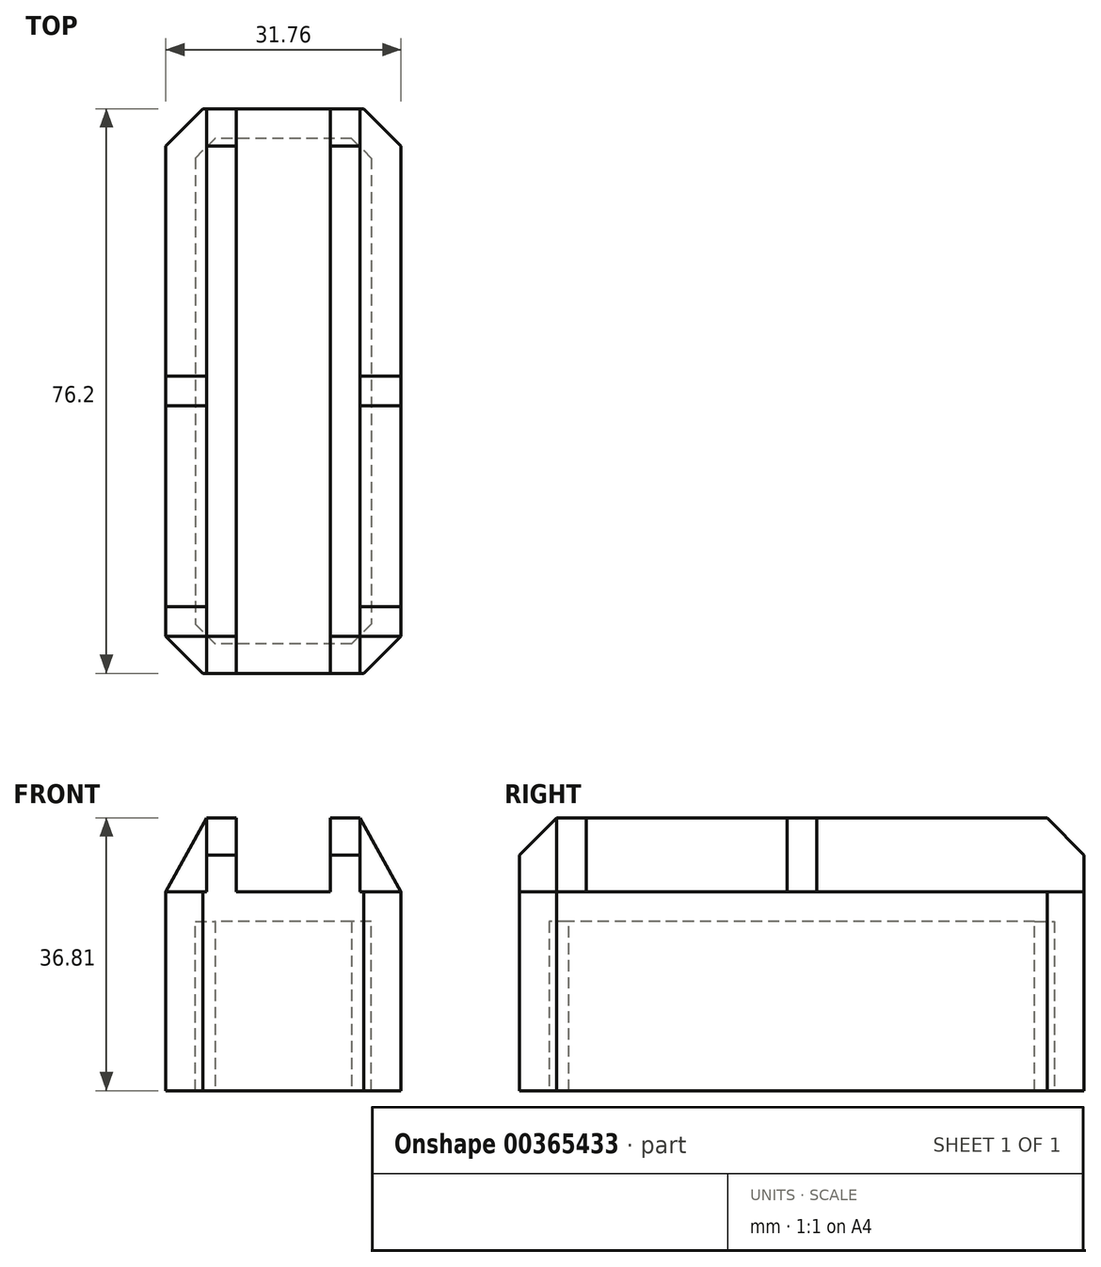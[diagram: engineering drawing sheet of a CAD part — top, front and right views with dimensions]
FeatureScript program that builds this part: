
annotation { "Feature Type Name" : "Feature", "Feature Type Description" : "" }
export const myFeature = defineFeature(function(context is Context, id is Id, definition is map)
    precondition{}
    {
        {
            var Q0;
            Q0=qCreatedBy(makeId("Top.planeOp"),FACE);
            var sketch = newSketch(context, id + "F0", { "sketchPlane" : qUnion([Q0])});
            skLineSegment(sketch, "E0.bottom", {"start": v(15.88, 38.1) * mm, "end": v(-15.87, 38.1) * mm});
            skLineSegment(sketch, "E0.top", {"start": v(15.87, -38.1) * mm, "end": v(-15.88, -38.1) * mm});
            skLineSegment(sketch, "E0.left", {"start": v(15.88, 38.1) * mm, "end": v(15.88, -38.1) * mm});
            skLineSegment(sketch, "E0.right", {"start": v(-15.87, 38.1) * mm, "end": v(-15.88, -38.1) * mm});
            skPoint(sketch, "E0.middle", {"position": v(0, 0) * mm});
            skSolve(sketch);
        }
        {
            var Q0;
            Q0=makeQuery(id+"F0.imprint","IMPRINT",FACE,{"disambiguationData":[TD([[makeQuery(id+"F0.imprint","IMPRINT",EDGE,{"derivedFrom":sQuery(id+"F0.wireOp",EDGE,"E0.bottom")}),1.0]])]});
            extrude(context, id + "F1", {"entities" : qUnion([Q0]), "oppositeDirection" : true, "depth" : 26.8 * mm});
        }
        {
            var Q0;
            Q0=makeQuery(id+"F1.opExtrude","SWEPT_EDGE",EDGE,{"disambiguationData":[OSD([sQuery(id+"F0.wireOp",EDGE,"E0.top"),sQuery(id+"F0.wireOp",EDGE,"E0.right")])]});
            var Q1;
            Q1=makeQuery(id+"F1.opExtrude","SWEPT_EDGE",EDGE,{"disambiguationData":[OSD([sQuery(id+"F0.wireOp",EDGE,"E0.top"),sQuery(id+"F0.wireOp",EDGE,"E0.left")])]});
            var Q2;
            Q2=makeQuery(id+"F1.opExtrude","SWEPT_EDGE",EDGE,{"disambiguationData":[OSD([sQuery(id+"F0.wireOp",EDGE,"E0.bottom"),sQuery(id+"F0.wireOp",EDGE,"E0.right")])]});
            var Q3;
            Q3=makeQuery(id+"F1.opExtrude","SWEPT_EDGE",EDGE,{"disambiguationData":[OSD([sQuery(id+"F0.wireOp",EDGE,"E0.bottom"),sQuery(id+"F0.wireOp",EDGE,"E0.left")])]});
            chamfer(context, id + "F2", {"entities" : qUnion([Q0, Q1, Q2, Q3]), "width" : 5 * mm, "tangentPropagation" : true});
        }
        {
            var Q0;
            Q0=makeQuery(id+"F1.opExtrude","CAP_FACE",FACE,{"disambiguationData":[OSD([sQuery(id+"F0.wireOp",EDGE,"E0.bottom"),sQuery(id+"F0.wireOp",EDGE,"E0.top"),sQuery(id+"F0.wireOp",EDGE,"E0.left"),sQuery(id+"F0.wireOp",EDGE,"E0.right")])],"isStart":false});
            shell(context, id + "F3", {"entities" : qUnion([Q0]), "thickness" : 4 * mm});
        }
        {
            var Q0;
            Q0=qCreatedBy(makeId("Front.planeOp"),FACE);
            var sketch = newSketch(context, id + "F4", { "sketchPlane" : qUnion([Q0])});
            skLineSegment(sketch, "E1.bottom", {"start": v(-10.35, 10) * mm, "end": v(-6.35, 10) * mm});
            skLineSegment(sketch, "E1.top", {"start": v(-10.35, 0) * mm, "end": v(-6.35, 0) * mm});
            skLineSegment(sketch, "E1.left", {"start": v(-10.35, 10) * mm, "end": v(-10.35, 0) * mm});
            skLineSegment(sketch, "E1.right", {"start": v(-6.35, 10) * mm, "end": v(-6.35, 0) * mm});
            skLineSegment(sketch, "E2", {"start": v(0, 9.11) * mm, "end": v(0, -8.98) * mm, "construction": true});
            skLineSegment(sketch, "E3.MirrorCS", {"start": v(10.35, 10) * mm, "end": v(6.35, 10) * mm});
            skLineSegment(sketch, "E4.MirrorCS", {"start": v(10.35, 10) * mm, "end": v(10.35, 0) * mm});
            skLineSegment(sketch, "E5.MirrorCS", {"start": v(6.35, 10) * mm, "end": v(6.35, 0) * mm});
            skLineSegment(sketch, "E6.MirrorCS", {"start": v(10.35, 0) * mm, "end": v(6.35, 0) * mm});
            skSolve(sketch);
        }
        {
            var Q0;
            Q0=makeQuery(id+"F4.imprint","IMPRINT",FACE,{"disambiguationData":[TD([[makeQuery(id+"F4.imprint","IMPRINT",EDGE,{"derivedFrom":sQuery(id+"F4.wireOp",EDGE,"E3.MirrorCS")}),1.0]])]});
            var Q1;
            Q1=makeQuery(id+"F4.imprint","IMPRINT",FACE,{"disambiguationData":[TD([[makeQuery(id+"F4.imprint","IMPRINT",EDGE,{"derivedFrom":sQuery(id+"F4.wireOp",EDGE,"E1.bottom")}),-1.0]])]});
            extrude(context, id + "F5", {"entities" : qUnion([Q0, Q1]), "operationType" : NewBodyOperationType.ADD, "endBound" : BoundingType.SYMMETRIC, "depth" : 76.2 * mm});
        }
        {
            var Q0;
            Q0=qCreatedBy(makeId("Front.planeOp"),FACE);
            var sketch = newSketch(context, id + "F6", { "sketchPlane" : qUnion([Q0])});
            skLineSegment(sketch, "E7", {"start": v(-10.35, 0) * mm, "end": v(-10.35, 10) * mm});
            skLineSegment(sketch, "E8", {"start": v(-10.35, 0) * mm, "end": v(-15.88, 0) * mm});
            skLineSegment(sketch, "E9", {"start": v(-10.35, 10) * mm, "end": v(-15.88, 0) * mm});
            skLineSegment(sketch, "E10", {"start": v(0, 0) * mm, "end": v(0, 13.7) * mm, "construction": true});
            skLineSegment(sketch, "E11.MirrorCS", {"start": v(10.35, 10) * mm, "end": v(15.88, 0) * mm});
            skLineSegment(sketch, "E12.MirrorCS", {"start": v(10.35, 0) * mm, "end": v(15.88, 0) * mm});
            skLineSegment(sketch, "E13.MirrorCS", {"start": v(10.35, 0) * mm, "end": v(10.35, 10) * mm});
            skSolve(sketch);
        }
        {
            var Q0;
            Q0=makeQuery(id+"F6.imprint","IMPRINT",FACE,{"disambiguationData":[TD([[makeQuery(id+"F6.imprint","IMPRINT",EDGE,{"derivedFrom":sQuery(id+"F6.wireOp",EDGE,"E7")}),1.0]])]});
            var Q1;
            Q1=makeQuery(id+"F6.imprint","IMPRINT",FACE,{"disambiguationData":[TD([[makeQuery(id+"F6.imprint","IMPRINT",EDGE,{"derivedFrom":sQuery(id+"F6.wireOp",EDGE,"E11.MirrorCS")}),-1.0]])]});
            extrude(context, id + "F7", {"entities" : qUnion([Q0, Q1]), "operationType" : NewBodyOperationType.ADD, "endBound" : BoundingType.SYMMETRIC, "depth" : 4 * mm});
        }
        {
            var Q0;
            Q0=qCreatedBy(makeId("Front.planeOp"),FACE);
            var Q1;
            {var subQ0=sQuery(id+"F0.wireOp",EDGE,"E0.right");var subQ1=sQuery(id+"F0.wireOp",EDGE,"E0.top");Q1=makeQuery(id+"F2.opChamfer","BLEND_VERTEX",VERTEX,{"blendedFrom":[makeQuery(id+"F1.opExtrude","SWEPT_EDGE",EDGE,{"disambiguationData":[OSD([subQ1,subQ0])]}),makeQuery(id+"F1.opExtrude","CAP_FACE",FACE,{"disambiguationData":[OSD([sQuery(id+"F0.wireOp",EDGE,"E0.bottom"),subQ1,sQuery(id+"F0.wireOp",EDGE,"E0.left"),subQ0])],"isStart":true}),makeQuery(id+"F1.opExtrude","SWEPT_FACE",FACE,{"disambiguationData":[OSD([subQ0])]})],"blendedInto":[makeQuery(id+"F1.opExtrude","CAP_FACE",FACE,{"disambiguationData":[OSD([sQuery(id+"F0.wireOp",EDGE,"E0.bottom"),subQ1,sQuery(id+"F0.wireOp",EDGE,"E0.left"),subQ0])],"isStart":true}),makeQuery(id+"F1.opExtrude","SWEPT_FACE",FACE,{"disambiguationData":[OSD([subQ0])]})]});}
            cPlane(context, id + "F8", {"entities" : qUnion([Q0, Q1]), "cplaneType" : CPlaneType.PLANE_POINT, "offset" : 25 * mm, "width" : 150 * mm, "height" : 150 * mm});
        }
        {
            var Q0;
            Q0=qCreatedBy(id+"F8.planeOp",FACE);
            var sketch = newSketch(context, id + "F9", { "sketchPlane" : qUnion([Q0])});
            skLineSegment(sketch, "E14.0", {"start": v(-10.35, 10) * mm, "end": v(-15.88, 0) * mm});
            skLineSegment(sketch, "E15.0", {"start": v(-10.35, 0) * mm, "end": v(-15.88, 0) * mm});
            skLineSegment(sketch, "E16.0", {"start": v(10.35, 0) * mm, "end": v(15.88, 0) * mm});
            skLineSegment(sketch, "E17.0", {"start": v(10.35, 0) * mm, "end": v(10.35, 10) * mm});
            skLineSegment(sketch, "E18.0", {"start": v(10.35, 10) * mm, "end": v(15.88, 0) * mm});
            skLineSegment(sketch, "E19.0", {"start": v(-10.35, 0) * mm, "end": v(-10.35, 10) * mm});
            skSolve(sketch);
        }
        {
            var Q0;
            Q0=makeQuery(id+"F9.imprint","IMPRINT",FACE,{"disambiguationData":[TD([[makeQuery(id+"F9.imprint","IMPRINT",EDGE,{"derivedFrom":sQuery(id+"F9.wireOp",EDGE,"E14.0")}),1.0]])]});
            var Q1;
            Q1=makeQuery(id+"F9.imprint","IMPRINT",FACE,{"disambiguationData":[TD([[makeQuery(id+"F9.imprint","IMPRINT",EDGE,{"derivedFrom":sQuery(id+"F9.wireOp",EDGE,"E16.0")}),1.0]])]});
            extrude(context, id + "F10", {"entities" : qUnion([Q0, Q1]), "operationType" : NewBodyOperationType.ADD, "oppositeDirection" : true, "depth" : 4 * mm});
        }
        {
            var Q0;
            Q0=makeQuery(id+"F5.opExtrude","CAP_EDGE",EDGE,{"disambiguationData":[OSD([sQuery(id+"F4.wireOp",EDGE,"E1.bottom")])],"isStart":false});
            var Q1;
            Q1=makeQuery(id+"F5.opExtrude","CAP_EDGE",EDGE,{"disambiguationData":[OSD([sQuery(id+"F4.wireOp",EDGE,"E3.MirrorCS")])],"isStart":false});
            var Q2;
            Q2=makeQuery(id+"F5.opExtrude","CAP_EDGE",EDGE,{"disambiguationData":[OSD([sQuery(id+"F4.wireOp",EDGE,"E1.bottom")])],"isStart":true});
            var Q3;
            Q3=makeQuery(id+"F5.opExtrude","CAP_EDGE",EDGE,{"disambiguationData":[OSD([sQuery(id+"F4.wireOp",EDGE,"E3.MirrorCS")])],"isStart":true});
            chamfer(context, id + "F11", {"entities" : qUnion([Q0, Q1, Q2, Q3]), "width" : 5 * mm, "tangentPropagation" : true});
        }
    });
